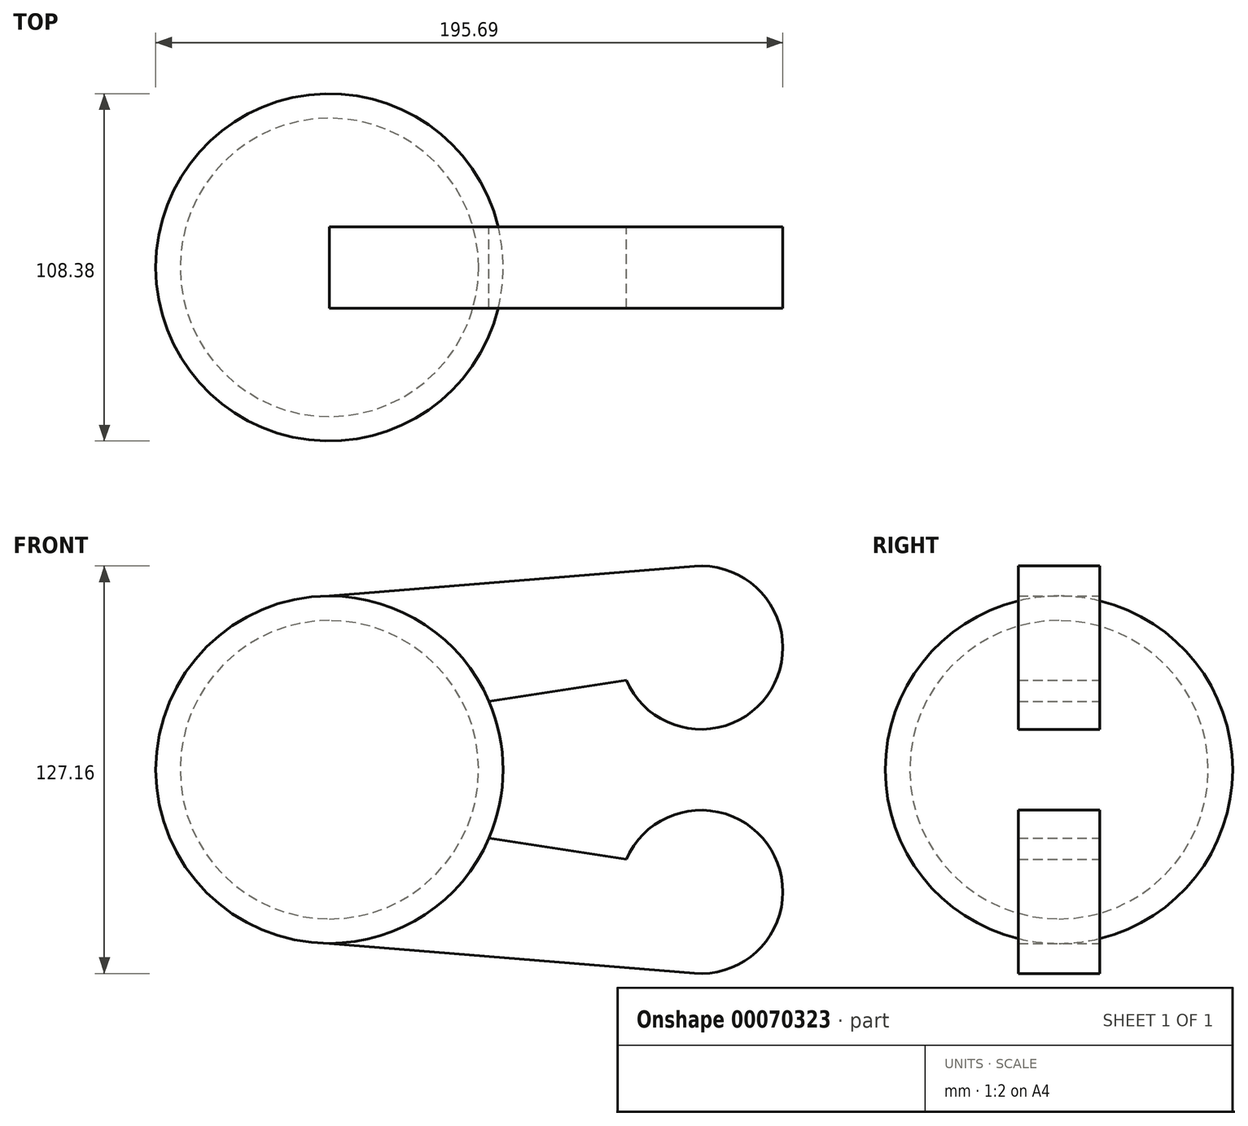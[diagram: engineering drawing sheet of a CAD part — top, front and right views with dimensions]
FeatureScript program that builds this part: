
annotation { "Feature Type Name" : "Feature", "Feature Type Description" : "" }
export const myFeature = defineFeature(function(context is Context, id is Id, definition is map)
    precondition{}
    {
        {
            var Q0;
            Q0=qCreatedBy(makeId("Front.planeOp"),FACE);
            var sketch = newSketch(context, id + "F0", { "sketchPlane" : qUnion([Q0])});
            skCircle(sketch, "E0", {"center": v(0, 0) * mm, "radius": 54.19 * mm});
            skCircle(sketch, "E1", {"center": v(116.02, 38.1) * mm, "radius": 25.48 * mm});
            skCircle(sketch, "E2", {"center": v(116.02, -38.1) * mm, "radius": 25.48 * mm});
            skLineSegment(sketch, "E3", {"start": v(0, 54.19) * mm, "end": v(113.94, 63.5) * mm});
            skLineSegment(sketch, "E4", {"start": v(0, -54.19) * mm, "end": v(113.94, -63.5) * mm});
            skLineSegment(sketch, "E5", {"start": v(49.8, 21.34) * mm, "end": v(92.64, 27.94) * mm});
            skLineSegment(sketch, "E6", {"start": v(49.8, -21.34) * mm, "end": v(92.64, -27.94) * mm});
            skCircle(sketch, "E7", {"center": v(0, 0) * mm, "radius": 46.57 * mm});
            skLineSegment(sketch, "E8", {"start": v(0, -54.19) * mm, "end": v(0, 54.19) * mm});
            skSolve(sketch);
        }
        {
            var Q0;
            {var subQ0=sQuery(id+"F0.wireOp",EDGE,"E4");Q0=makeQuery(id+"F0.imprint","IMPRINT",FACE,{"disambiguationData":[TD([[makeQuery(id+"F0.imprint","IMPRINT",EDGE,{"derivedFrom":subQ0}),1.0]])]});}
            var Q1;
            {var subQ0=sQuery(id+"F0.wireOp",EDGE,"E2");var subQ1=makeQuery(id+"F0.imprint","INTERSECT",VERTEX,{"derivedFrom":[subQ0,sQuery(id+"F0.wireOp",EDGE,"E4")]});Q1=makeQuery(id+"F0.imprint","IMPRINT",FACE,{"disambiguationData":[TD([[makeQuery(id+"F0.imprint","IMPRINT",EDGE,{"disambiguationData":[TD([[subQ1,1.0]])],"derivedFrom":subQ0}),1.0]])]});}
            var Q2;
            {var subQ0=sQuery(id+"F0.wireOp",EDGE,"E1");var subQ1=makeQuery(id+"F0.imprint","INTERSECT",VERTEX,{"derivedFrom":[subQ0,sQuery(id+"F0.wireOp",EDGE,"E3")]});Q2=makeQuery(id+"F0.imprint","IMPRINT",FACE,{"disambiguationData":[TD([[makeQuery(id+"F0.imprint","IMPRINT",EDGE,{"disambiguationData":[TD([[subQ1,-1.0]])],"derivedFrom":subQ0}),1.0]])]});}
            var Q3;
            {var subQ0=sQuery(id+"F0.wireOp",EDGE,"E3");Q3=makeQuery(id+"F0.imprint","IMPRINT",FACE,{"disambiguationData":[TD([[makeQuery(id+"F0.imprint","IMPRINT",EDGE,{"derivedFrom":subQ0}),-1.0]])]});}
            extrude(context, id + "F1", {"entities" : qUnion([Q0, Q1, Q2, Q3]), "endBound" : BoundingType.SYMMETRIC, "depth" : 25.4 * mm});
        }
        {
            var Q0;
            {var subQ0=sQuery(id+"F0.wireOp",EDGE,"E8");var subQ4=sQuery(id+"F0.wireOp",EDGE,"E7");var subQ6=makeQuery(id+"F0.imprint","INTERSECT",VERTEX,{"disambiguationData":[OD(0.0)],"derivedFrom":[subQ4,subQ0]});Q0=makeQuery(id+"F0.imprint","IMPRINT",FACE,{"disambiguationData":[TD([[makeQuery(id+"F0.imprint","IMPRINT",EDGE,{"disambiguationData":[TD([[subQ6,1.0]])],"derivedFrom":subQ4}),-1.0]])]});}
            var Q1;
            Q1=sQuery(id+"F0.wireOp",EDGE,"E8");
            revolve(context, id + "F2", {"entities" : qUnion([Q0]), "axis" : qUnion([Q1]), "revolveType" : RevolveType.FULL});
        }
    });
